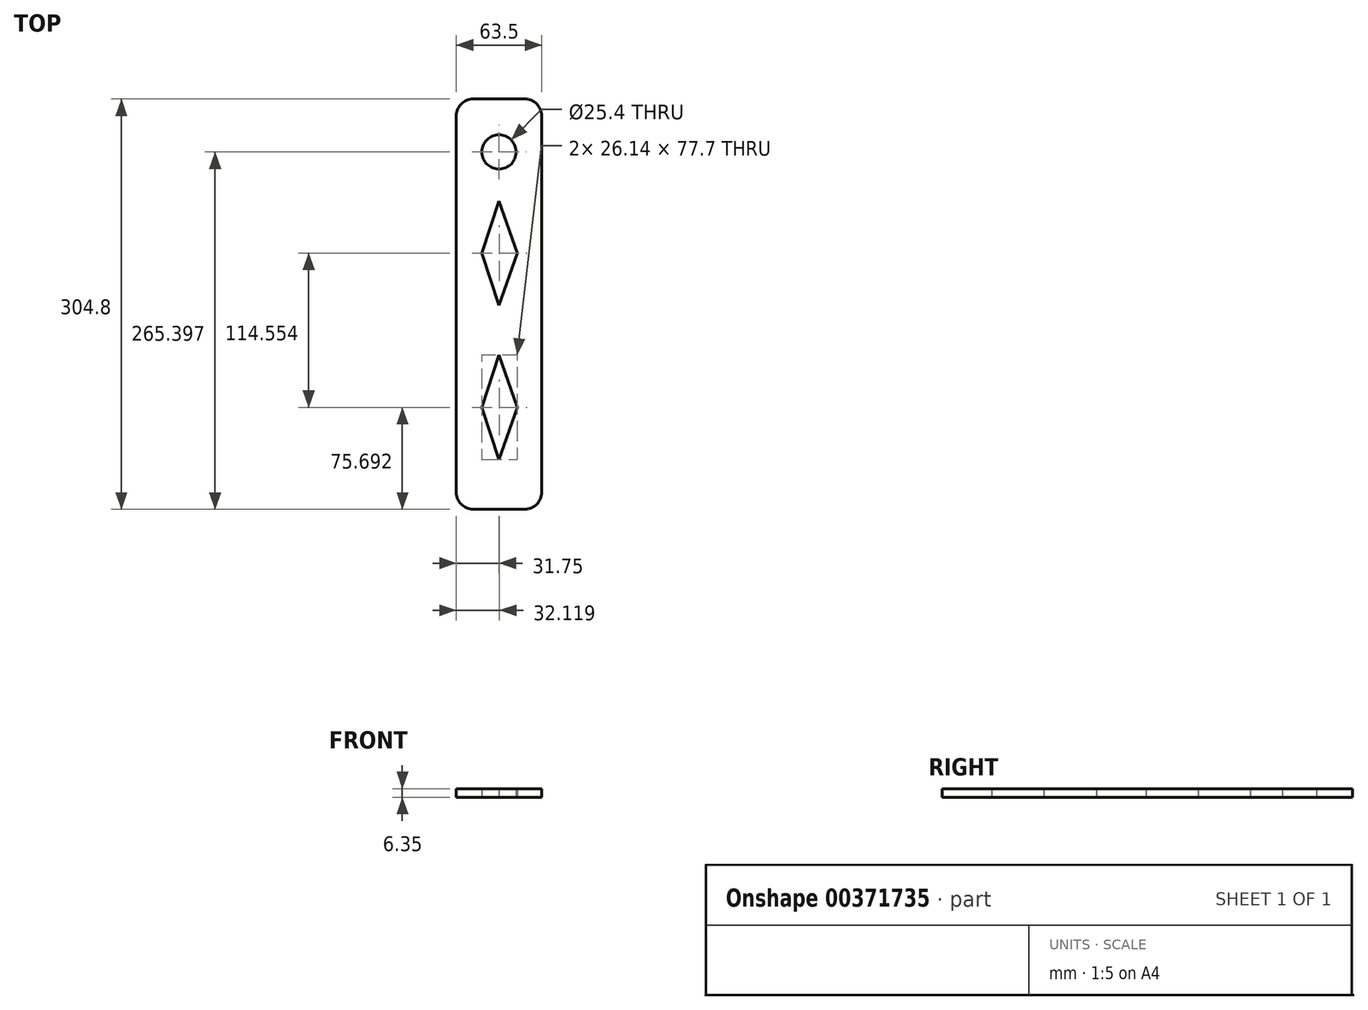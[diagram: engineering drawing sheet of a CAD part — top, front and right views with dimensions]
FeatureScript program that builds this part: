
annotation { "Feature Type Name" : "Feature", "Feature Type Description" : "" }
export const myFeature = defineFeature(function(context is Context, id is Id, definition is map)
    precondition{}
    {
        {
            var Q0;
            Q0=qCreatedBy(makeId("Top.planeOp"),FACE);
            var sketch = newSketch(context, id + "F0", { "sketchPlane" : qUnion([Q0])});
            skLineSegment(sketch, "E0.bottom", {"start": v(12.7, 0) * mm, "end": v(50.8, 0) * mm});
            skLineSegment(sketch, "E0.top", {"start": v(12.7, 304.8) * mm, "end": v(50.8, 304.8) * mm});
            skLineSegment(sketch, "E0.left", {"start": v(0, 12.7) * mm, "end": v(0, 292.1) * mm});
            skLineSegment(sketch, "E0.right", {"start": v(63.5, 12.7) * mm, "end": v(63.5, 292.1) * mm});
            skLineSegment(sketch, "E1.0.1.0", {"start": v(31.75, 229.1) * mm, "end": v(45.19, 190.25) * mm});
            skLineSegment(sketch, "E1.0.1.1", {"start": v(19.05, 190.25) * mm, "end": v(31.75, 229.1) * mm});
            skLineSegment(sketch, "E1.0.1.2", {"start": v(31.75, 151.4) * mm, "end": v(19.05, 190.25) * mm});
            skLineSegment(sketch, "E1.0.1.3", {"start": v(45.19, 190.25) * mm, "end": v(31.75, 151.4) * mm});
            skLineSegment(sketch, "E1.0.2.0", {"start": v(31.75, 114.54) * mm, "end": v(45.19, 75.7) * mm});
            skLineSegment(sketch, "E1.0.2.1", {"start": v(19.05, 75.7) * mm, "end": v(31.75, 114.54) * mm});
            skLineSegment(sketch, "E1.0.2.2", {"start": v(31.75, 36.84) * mm, "end": v(19.05, 75.7) * mm});
            skLineSegment(sketch, "E1.0.2.3", {"start": v(45.19, 75.7) * mm, "end": v(31.75, 36.84) * mm});
            skPoint(sketch, "E2.visualSharp", {"position": v(0, 304.8) * mm});
            skArc(sketch, "E2.filletArc", {"start": v(12.7, 304.8) * mm, "mid": v(3.72, 301.08) * mm, "end": v(0, 292.1) * mm});
            skPoint(sketch, "E3.visualSharp", {"position": v(63.5, 304.8) * mm});
            skArc(sketch, "E3.filletArc", {"start": v(63.5, 292.1) * mm, "mid": v(59.78, 301.08) * mm, "end": v(50.8, 304.8) * mm});
            skPoint(sketch, "E4.visualSharp", {"position": v(0, 0) * mm});
            skArc(sketch, "E4.filletArc", {"start": v(0, 12.7) * mm, "mid": v(3.72, 3.72) * mm, "end": v(12.7, 0) * mm});
            skPoint(sketch, "E5.visualSharp", {"position": v(63.5, 0) * mm});
            skArc(sketch, "E5.filletArc", {"start": v(50.8, 0) * mm, "mid": v(59.78, 3.72) * mm, "end": v(63.5, 12.7) * mm});
            skCircle(sketch, "E6", {"center": v(31.75, 265.4) * mm, "radius": 12.7 * mm});
            skSolve(sketch);
        }
        {
            var Q0;
            Q0=makeQuery(id+"F0.imprint","IMPRINT",FACE,{"disambiguationData":[TD([[makeQuery(id+"F0.imprint","IMPRINT",EDGE,{"derivedFrom":sQuery(id+"F0.wireOp",EDGE,"E0.bottom")}),1.0]])]});
            extrude(context, id + "F1", {"entities" : qUnion([Q0]), "depth" : 6.35 * mm});
        }
    });
